# Revit family: 1157xxx Tosca LED (Cord Set)
name_source: partatom
category: Lighting Fixtures
units: mm (PartAtom-declared; Revit-internal decimal feet)

## family parameters
Always vertical = Yes
Cut with Voids When Loaded = No
Host = Wall
Light Source = Yes
OmniClass Number = 23.80.70.00
OmniClass Title = Lighting
Part Type = Normal
Room Calculation Point = No
Round Connector Dimension = Use Diameter
Shared = No

## types (2) — shared parameters
Color Filter = 16777215
Dimming Lamp Color Temperature Shift = <None>
Driver Required = No
Main Material = Metal - Steel
Manufacturer = Astro Lighting Ltd
Manufacturer URL - Europe and Rest of World = www.astrolighting.com
Manufacturer URL - North America = us.astrolighting.com
URL = www.astrolighting.com
zero-valued in all types: Default Elevation

## per-type parameters (varying)
| type | ADA compliant | Dimmable | Dimming Method | Driver Included | Efficacy (lm/w) | Electrical Class | Emit from Line Length | Lamp | Light Source Fixed | Location / IP Rating | Main Finish | Photometric Web File | Power (Watts) | Product CCT | Product CRI | Product Dimensions (MM) | Product Location | Product SKU | Product Weight (KG) | Tilt Angle |
| CE | N / A | No | Not Applicable | Yes | 32 | 1 | 1 mm  [stored 0.00328084 ft] | LED | Yes | IP20 | Various | 1157013_Tosca LED UL_Photometry_IES_Iss.01.ies | 1 | 2700 | 90 | 200 x 45 x 43 | Indoor | 1157020 | 1.450 | 90.00° |
| ETL |  |  |  |  |  | 0 | 610 mm |  |  | DAMP |  | generic |  | 2700K / 3000K | 80 / 90 |  | Bathroom | 1234001 |  | 60.00° |

note: [stored X ft] marks values corroborated as IEEE doubles in the binary element streams (Revit-internal decimal feet)

## geometry (parser evidence)
native form markers: Sweep x3
no freeform markers — native parametric forms only
